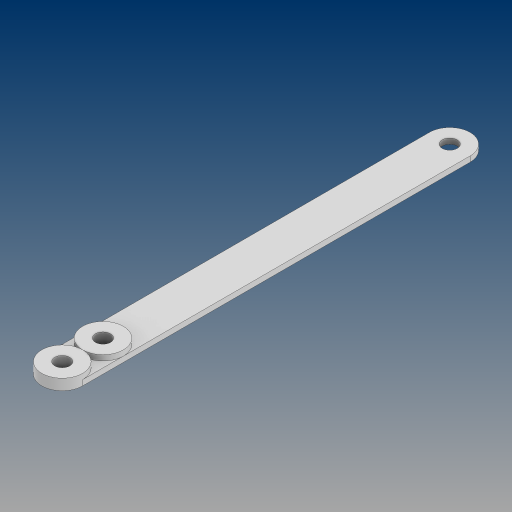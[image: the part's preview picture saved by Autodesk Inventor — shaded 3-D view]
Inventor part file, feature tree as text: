
AUTODESK INVENTOR PART (.ipt)
format: ipt  version: 2023 (Build 270158000, 158)  size: 124,416 bytes
history: native  units: mm
features: extrude x4
ambient origin geometry x8: Origin, YZ Plane, XZ Plane, XY Plane, X Axis, Y Axis, Z Axis, Center Point
bodies: Solid1 (feature_tree)
feature tree (4):
  extrude  "Extrusion1"  Depth=15.0mm
  extrude  "Extrusion2"  Depth=30.0mm
  extrude  "Extrusion3"  Depth=157.681217mm
  extrude  "Extrusion4"  TaperAngle=90.0deg  [1 undecoded]
note: 1 required parameter value undecoded (feature->parameter linkage not recoverable at this tier; creation-order binding heuristic only, values carry confidence <= 0.55)
